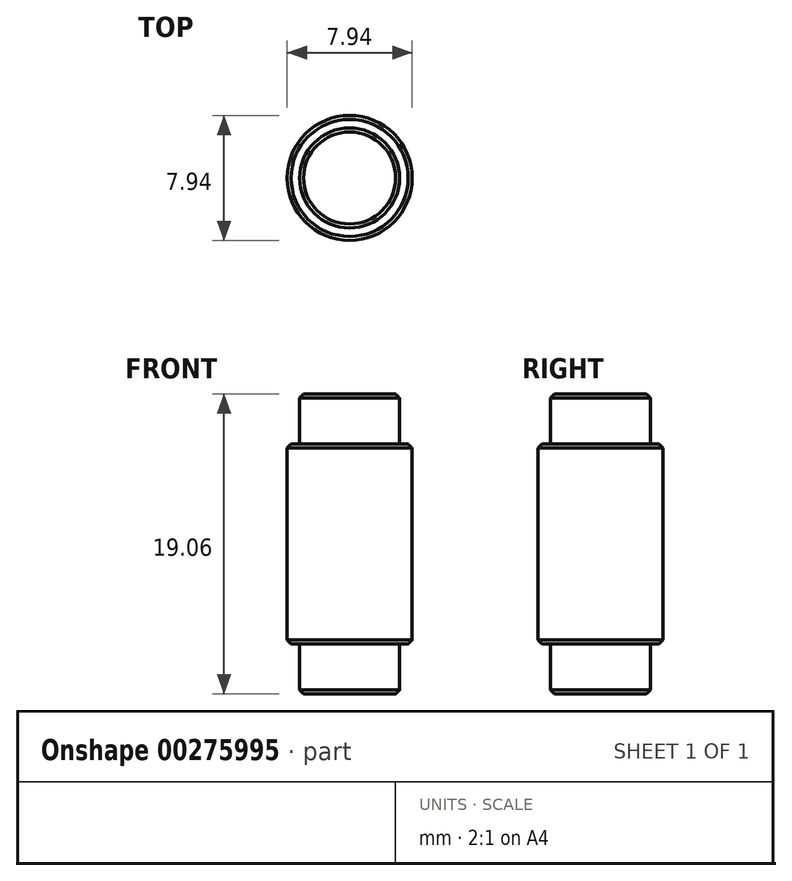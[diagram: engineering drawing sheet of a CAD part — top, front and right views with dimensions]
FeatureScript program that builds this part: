
annotation { "Feature Type Name" : "Feature", "Feature Type Description" : "" }
export const myFeature = defineFeature(function(context is Context, id is Id, definition is map)
    precondition{}
    {
        {
            var Q0;
            Q0=qCreatedBy(makeId("Top.planeOp"),FACE);
            var sketch = newSketch(context, id + "F0", { "sketchPlane" : qUnion([Q0])});
            skCircle(sketch, "E0", {"center": v(0, 0) * mm, "radius": 3.97 * mm});
            skSolve(sketch);
        }
        {
            var Q0;
            Q0=makeQuery(id+"F0.imprint","IMPRINT",FACE,{"disambiguationData":[TD([[makeQuery(id+"F0.imprint","IMPRINT",EDGE,{"derivedFrom":sQuery(id+"F0.wireOp",EDGE,"E0")}),1.0]])]});
            extrude(context, id + "F1", {"entities" : qUnion([Q0]), "depth" : 12.7 * mm});
        }
        {
            var Q0;
            Q0=qCreatedBy(makeId("Top.planeOp"),FACE);
            var sketch = newSketch(context, id + "F2", { "sketchPlane" : qUnion([Q0])});
            skCircle(sketch, "E1", {"center": v(0, 0) * mm, "radius": 3.18 * mm});
            skSolve(sketch);
        }
        {
            var Q0;
            Q0=qSketchRegion(id+"F2",true);
            extrude(context, id + "F3", {"entities" : qUnion([Q0]), "operationType" : NewBodyOperationType.ADD, "oppositeDirection" : true, "depth" : 3.17 * mm});
        }
        {
            var Q0;
            Q0=makeQuery(id+"F1.opExtrude","CAP_FACE",FACE,{"disambiguationData":[OSD([sQuery(id+"F0.wireOp",EDGE,"E0")])],"isStart":false});
            var sketch = newSketch(context, id + "F4", { "sketchPlane" : qUnion([Q0])});
            skCircle(sketch, "E2", {"center": v(0, 0) * mm, "radius": 3.18 * mm});
            skSolve(sketch);
        }
        {
            var Q0;
            Q0=qSketchRegion(id+"F4",true);
            extrude(context, id + "F5", {"entities" : qUnion([Q0]), "operationType" : NewBodyOperationType.ADD, "depth" : 3.17 * mm});
        }
        {
            var Q0;
            Q0=makeQuery(id+"F5.opExtrude","CAP_EDGE",EDGE,{"disambiguationData":[OSD([sQuery(id+"F4.wireOp",EDGE,"E2")])],"isStart":false});
            var Q1;
            Q1=makeQuery(id+"F1.opExtrude","CAP_EDGE",EDGE,{"disambiguationData":[OSD([sQuery(id+"F0.wireOp",EDGE,"E0")])],"isStart":false});
            var Q2;
            Q2=makeQuery(id+"F1.opExtrude","CAP_EDGE",EDGE,{"disambiguationData":[OSD([sQuery(id+"F0.wireOp",EDGE,"E0")])],"isStart":true});
            var Q3;
            Q3=makeQuery(id+"F3.opExtrude","CAP_EDGE",EDGE,{"disambiguationData":[OSD([sQuery(id+"F2.wireOp",EDGE,"E1")])],"isStart":false});
            chamfer(context, id + "F6", {"entities" : qUnion([Q0, Q1, Q2, Q3]), "width" : 0.25 * mm, "tangentPropagation" : true});
        }
    });
